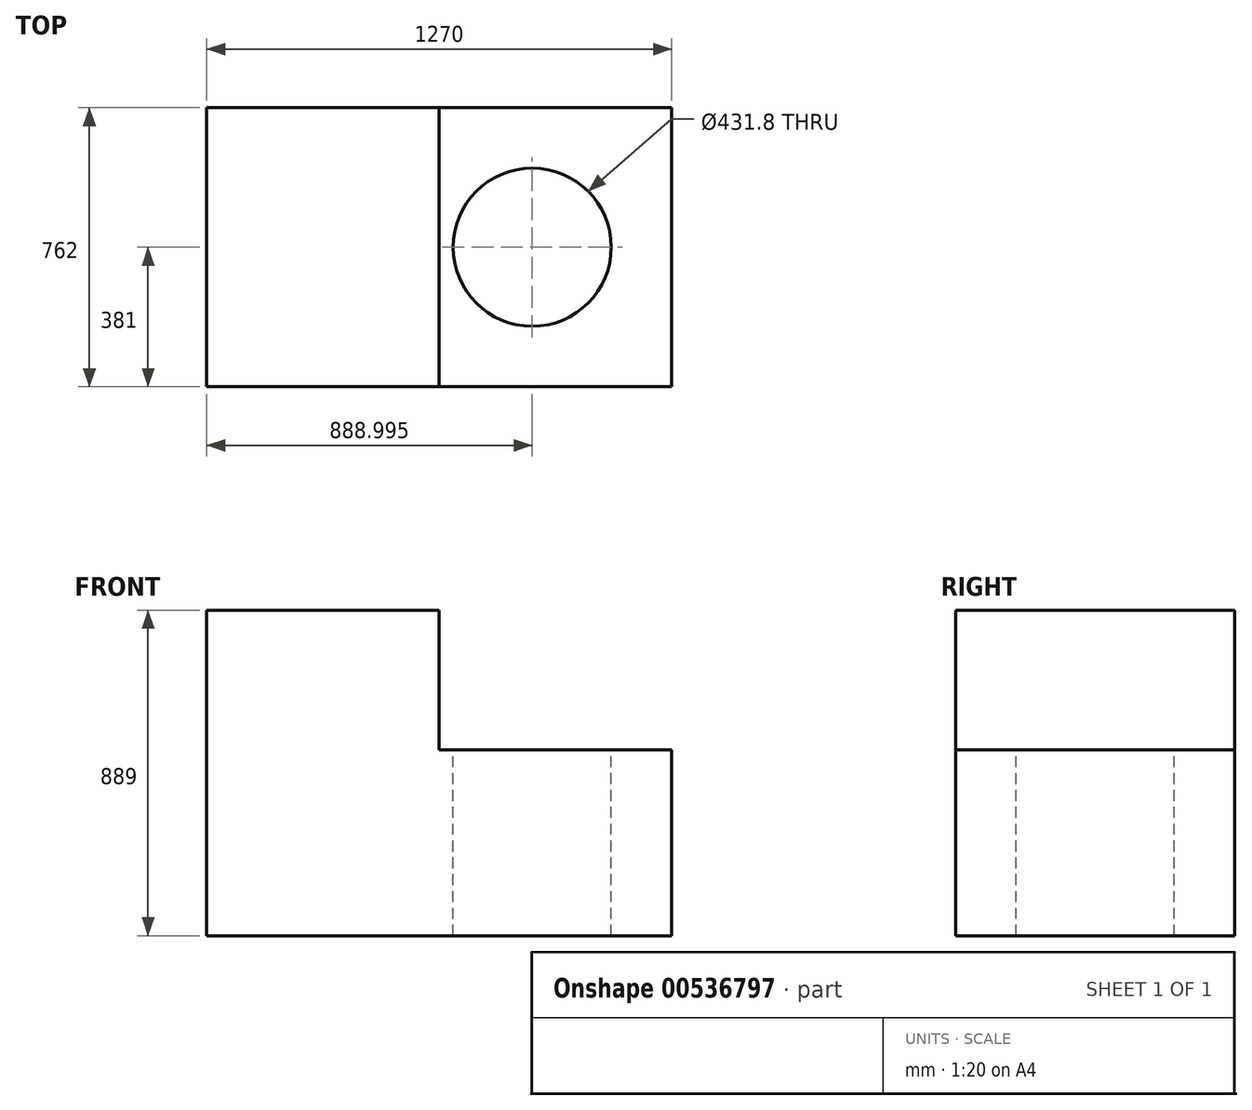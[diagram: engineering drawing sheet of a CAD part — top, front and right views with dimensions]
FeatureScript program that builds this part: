
annotation { "Feature Type Name" : "Feature", "Feature Type Description" : "" }
export const myFeature = defineFeature(function(context is Context, id is Id, definition is map)
    precondition{}
    {
        {
            var Q0;
            Q0=qCreatedBy(makeId("Front.planeOp"),FACE);
            var sketch = newSketch(context, id + "F0", { "sketchPlane" : qUnion([Q0])});
            skLineSegment(sketch, "E0", {"start": v(-70.04, 433.4) * mm, "end": v(-70.04, -455.6) * mm});
            skLineSegment(sketch, "E1", {"start": v(-70.04, -455.6) * mm, "end": v(1199.96, -455.6) * mm});
            skLineSegment(sketch, "E2", {"start": v(1199.96, -455.6) * mm, "end": v(1199.96, 52.4) * mm});
            skLineSegment(sketch, "E3", {"start": v(-70.04, 433.4) * mm, "end": v(564.96, 433.4) * mm});
            skLineSegment(sketch, "E4", {"start": v(564.96, 433.4) * mm, "end": v(564.96, 52.4) * mm});
            skLineSegment(sketch, "E5", {"start": v(564.96, 52.4) * mm, "end": v(1199.96, 52.4) * mm});
            skSolve(sketch);
        }
        {
            var Q0;
            Q0=makeQuery(id+"F0.imprint","IMPRINT",FACE,{"disambiguationData":[TD([[makeQuery(id+"F0.imprint","IMPRINT",EDGE,{"derivedFrom":sQuery(id+"F0.wireOp",EDGE,"E0")}),1.0]])]});
            extrude(context, id + "F1", {"entities" : qUnion([Q0]), "depth" : 762 * mm, "offsetDistance" : 25.4 * mm});
        }
        {
            var Q0;
            Q0=makeQuery(id+"F1.opExtrude","SWEPT_FACE",FACE,{"disambiguationData":[OSD([sQuery(id+"F0.wireOp",EDGE,"E5")])]});
            var sketch = newSketch(context, id + "F2", { "sketchPlane" : qUnion([Q0])});
            skCircle(sketch, "E6", {"center": v(818.96, -381) * mm, "radius": 215.9 * mm});
            skSolve(sketch);
        }
        {
            var Q0;
            Q0 = qSketchRegion(id + "F2", true);
            extrude(context, id + "F3", {"entities" : qUnion([Q0]), "operationType" : NewBodyOperationType.REMOVE, "oppositeDirection" : true, "depth" : 508 * mm, "offsetDistance" : 25.4 * mm});
        }
    });
